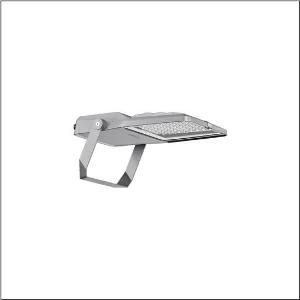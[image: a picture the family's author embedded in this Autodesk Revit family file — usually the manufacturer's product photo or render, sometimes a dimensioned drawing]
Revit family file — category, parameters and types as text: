
# Revit family: floodlight_fl_21_iq_mini___pl33t_5xa7771c2f1a_64ec
name_source: partatom
category: Lighting Fixtures
units: mm (PartAtom-declared; Revit-internal decimal feet)

## family parameters
Cut with Voids When Loaded = No
Host = Face
Light Source = No
Part Type = Normal
Room Calculation Point = No
Round Connector Dimension = Use Diameter
Shared = No

## types (1)
- --- (1 x LED, 12060 lm, 87.2 W, 3000K)
    Apparent Load = 87 VA
    CIE Flux Codes = 26 75 99 100 100
    Color Rendering = 70
    Color Temperature = 3000K
    Default Elevation = 1800 mm
    Description = Floodlight FL 21 iQ mini, floodlight, primary light control with lens, of PMMA, primary optical cover: protective disc, of toughened safety glass, transparent, light distribution: PL33T, light emission: direct distribution, installation type: surface-mounted, lamps: LED, High Power LED, rated values: 12.060lm | 87,2W | 138,3lm/W (begin service life); end service life: 12.060lm | 92,1W; at 50% lumin. flux: 6.030lm | 40,1W | 150,4lm/W, colour temperature: 3000K, colour rendering: CRI > 70, light colour: 730, light setting 1 begin service life: 100% | 12.060lm | 87,2W | 138,3lm/W | 3.000K, light setting 1 end service life: 92,1W, further light settings possible, control: Auto-Match, Temp-Guard, Lumen-Switch, Night-Set, Smart-Wire, Light-Fading, Desk-Remote (wireless, voltage-free reading and setting of iQ features in the workshop via application-optimized NFC function/RFID function), optimised constant luminous flux control (CLO 2.0), pre-setting: linear dimming characteristic, with terminal, 6-pole, mains connection: 220..240V, AC, 50/60Hz, luminaire housing, of diecast aluminium, powder-coated, SITECO metallic grey (DB 702S), corrosivity category C5 mid according to DIN EN ISO 12944suitable for swimming poolschlorine-resistant, sealing non-destructively replaceable, mounting bracket, of steel, galvanised, powder-coated, SITECO metallic grey (DB 702S), protection rating (complete): IP66, insulation class (complete): insulation class II (safety insulation), certification: CE, ENEC, VDE, protection symbol: D, impact resistance: IK08, permissible operating ambient temperature: -40..+40°C, permissible operating ambient temperature for outdoor applications: -40..+50°C, standard: DIN EN 12944, LABS conformity tested according to VDMA 24364:2018-05, packaging unit: 1 piece

Light Distribution: PL33T
    Height = 70 mm
    Lamp = 1 x LED
    Lamp Light Flux = 12060 lm
    Lamp Power = 87.2 W
    Lamp count = 1
    Length = 485 mm
    Luminous efficacy = 138 lm/W
    Manufacturer = Siteco
    ModVariant = No
    Model = 5XA7771C2F1A
    Mounting Place = Pole
    Mounting Type = Pole annexe
    Number of Poles = 1
    OnlyDefault = Yes
    Power Factor = 1
    Product Name = Floodlight FL 21 iQ mini | PL33T
    Product group = floodlight | pylon annexe
    ProductGroupID = 6201
    Protection Class = Protection class II
    Protection Degree = IP 66
    RLX_Detail_Level = 1
    RLX_Emergency_Light_Flux = 0 lm
    RLX_Emergency_Type = 0
    RLX_Emergency_Type_DB = No
    RlxData = <blob elided: 96537 chars, md5=3f168be6>
    Socket = socket
    Standby Power = 0 W
    System Light Flux = 12060 lm
    System Power = 87 W
    Type Comments = factory setting: luminous flux: 100 % | dim-lin: 254 | 456 mA
    Type Image = l_1006845.jpg
    URL = http://relux.com
    VarID = @adj_150867
    Voltage = 0 V
    Weight = 0.00 kg
    Width = 337 mm

## geometry (parser evidence)
native form markers: Blend x4, Sweep x13
no freeform markers — native parametric forms only
